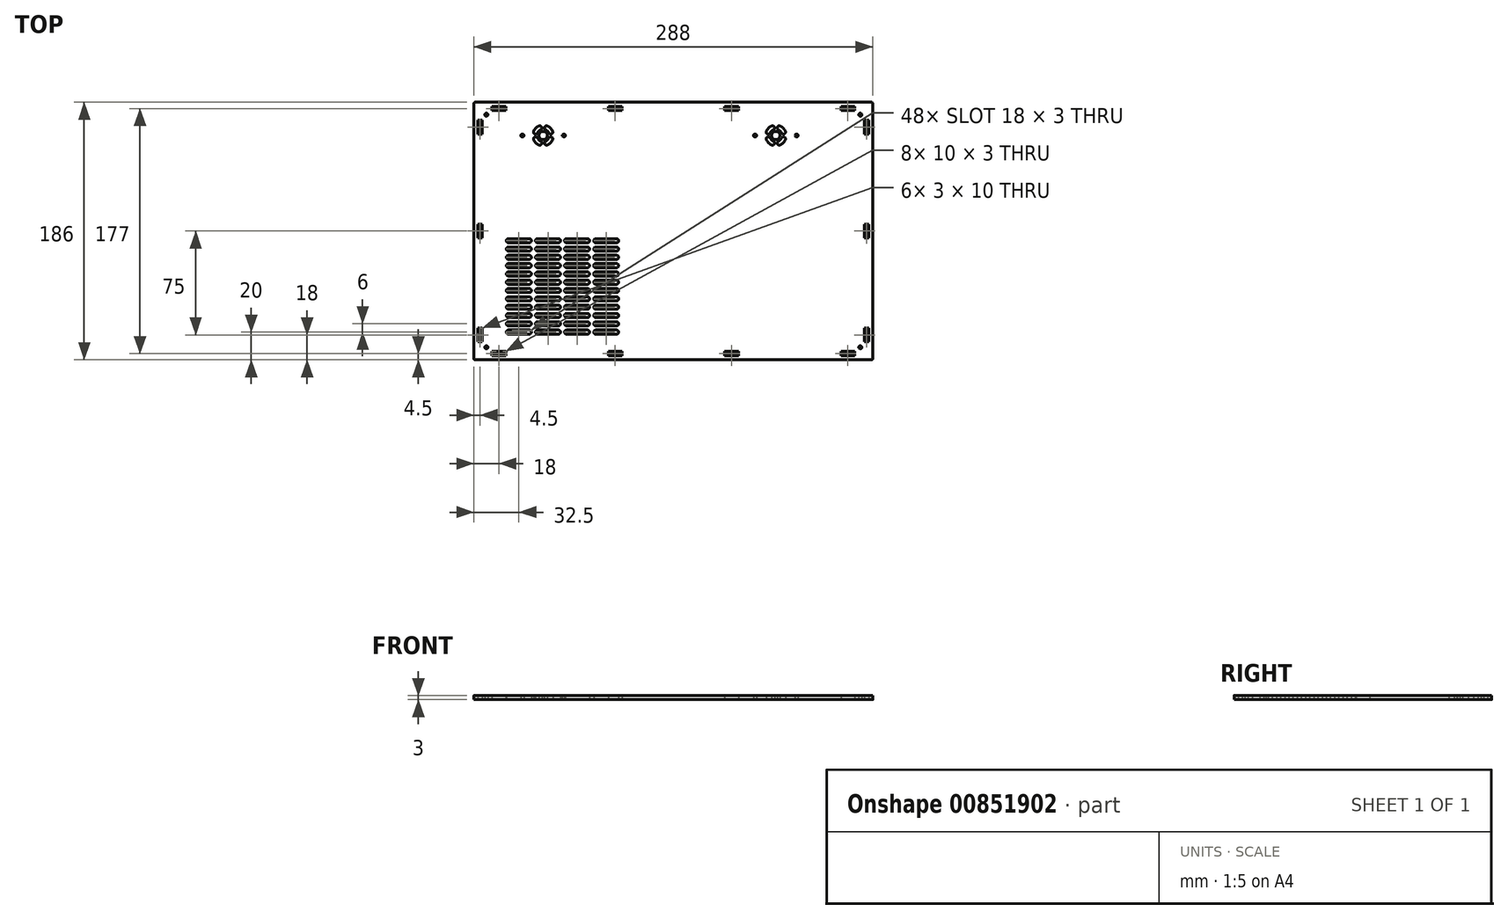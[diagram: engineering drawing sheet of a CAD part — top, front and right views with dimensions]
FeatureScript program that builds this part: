
annotation { "Feature Type Name" : "Feature", "Feature Type Description" : "" }
export const myFeature = defineFeature(function(context is Context, id is Id, definition is map)
    precondition{}
    {
        {
            var Q0;
            Q0=qCreatedBy(makeId("Top.planeOp"),FACE);
            var sketch = newSketch(context, id + "F0", { "sketchPlane" : qUnion([Q0])});
            skLineSegment(sketch, "E0.bottom", {"start": v(0, 0) * mm, "end": v(297, 0) * mm, "construction": true});
            skLineSegment(sketch, "E0.top", {"start": v(0, 210) * mm, "end": v(297, 210) * mm, "construction": true});
            skLineSegment(sketch, "E0.left", {"start": v(0, 0) * mm, "end": v(0, 210) * mm, "construction": true});
            skLineSegment(sketch, "E0.right", {"start": v(297, 0) * mm, "end": v(297, 210) * mm, "construction": true});
            skLineSegment(sketch, "E1", {"start": v(6, 5) * mm, "end": v(292, 5) * mm});
            skLineSegment(sketch, "E2", {"start": v(293, 6) * mm, "end": v(293, 190) * mm});
            skLineSegment(sketch, "E3", {"start": v(292, 191) * mm, "end": v(6, 191) * mm});
            skLineSegment(sketch, "E4", {"start": v(5, 190) * mm, "end": v(5, 6) * mm});
            skLineSegment(sketch, "E5", {"start": v(18, 8) * mm, "end": v(28, 8) * mm});
            skLineSegment(sketch, "E6", {"start": v(28, 8) * mm, "end": v(28, 11) * mm});
            skLineSegment(sketch, "E7", {"start": v(28, 11) * mm, "end": v(18, 11) * mm});
            skLineSegment(sketch, "E8", {"start": v(18, 11) * mm, "end": v(18, 8) * mm});
            skLineSegment(sketch, "E9", {"start": v(102, 8) * mm, "end": v(112, 8) * mm});
            skLineSegment(sketch, "E10", {"start": v(112, 8) * mm, "end": v(112, 11) * mm});
            skLineSegment(sketch, "E11", {"start": v(112, 11) * mm, "end": v(102, 11) * mm});
            skLineSegment(sketch, "E12", {"start": v(102, 11) * mm, "end": v(102, 8) * mm});
            skLineSegment(sketch, "E13", {"start": v(8, 18) * mm, "end": v(11, 18) * mm});
            skLineSegment(sketch, "E14", {"start": v(11, 18) * mm, "end": v(11, 28) * mm});
            skLineSegment(sketch, "E15", {"start": v(11, 28) * mm, "end": v(8, 28) * mm});
            skLineSegment(sketch, "E16", {"start": v(8, 28) * mm, "end": v(8, 18) * mm});
            skLineSegment(sketch, "E17", {"start": v(149, 5) * mm, "end": v(149, 191) * mm, "construction": true});
            skLineSegment(sketch, "E18", {"start": v(5, 98) * mm, "end": v(293, 98) * mm, "construction": true});
            skLineSegment(sketch, "E19", {"start": v(8, 98) * mm, "end": v(8, 93) * mm});
            skLineSegment(sketch, "E20", {"start": v(8, 93) * mm, "end": v(11, 93) * mm});
            skLineSegment(sketch, "E21", {"start": v(11, 93) * mm, "end": v(11, 98) * mm});
            skLineSegment(sketch, "E22.MirrorCS", {"start": v(186, 11) * mm, "end": v(196, 11) * mm});
            skLineSegment(sketch, "E23.MirrorCS", {"start": v(186, 8) * mm, "end": v(186, 11) * mm});
            skLineSegment(sketch, "E24.MirrorCS", {"start": v(196, 8) * mm, "end": v(186, 8) * mm});
            skLineSegment(sketch, "E25.MirrorCS", {"start": v(196, 11) * mm, "end": v(196, 8) * mm});
            skLineSegment(sketch, "E26.MirrorCS", {"start": v(270, 8) * mm, "end": v(270, 11) * mm});
            skLineSegment(sketch, "E27.MirrorCS", {"start": v(270, 11) * mm, "end": v(280, 11) * mm});
            skLineSegment(sketch, "E28.MirrorCS", {"start": v(280, 8) * mm, "end": v(270, 8) * mm});
            skLineSegment(sketch, "E29.MirrorCS", {"start": v(280, 11) * mm, "end": v(280, 8) * mm});
            skLineSegment(sketch, "E30.MirrorCS", {"start": v(290, 18) * mm, "end": v(287, 18) * mm});
            skLineSegment(sketch, "E31.MirrorCS", {"start": v(287, 18) * mm, "end": v(287, 28) * mm});
            skLineSegment(sketch, "E32.MirrorCS", {"start": v(290, 28) * mm, "end": v(290, 18) * mm});
            skLineSegment(sketch, "E33.MirrorCS", {"start": v(287, 28) * mm, "end": v(290, 28) * mm});
            skLineSegment(sketch, "E34.MirrorCS", {"start": v(290, 98) * mm, "end": v(290, 93) * mm});
            skLineSegment(sketch, "E35.MirrorCS", {"start": v(290, 93) * mm, "end": v(287, 93) * mm});
            skLineSegment(sketch, "E36.MirrorCS", {"start": v(287, 93) * mm, "end": v(287, 98) * mm});
            skLineSegment(sketch, "E37.MirrorCS", {"start": v(8, 98) * mm, "end": v(8, 103) * mm});
            skLineSegment(sketch, "E38.MirrorCS", {"start": v(8, 103) * mm, "end": v(11, 103) * mm});
            skLineSegment(sketch, "E39.MirrorCS", {"start": v(11, 103) * mm, "end": v(11, 98) * mm});
            skLineSegment(sketch, "E40.MirrorCS", {"start": v(11, 168) * mm, "end": v(8, 168) * mm});
            skLineSegment(sketch, "E41.MirrorCS", {"start": v(11, 178) * mm, "end": v(11, 168) * mm});
            skLineSegment(sketch, "E42.MirrorCS", {"start": v(8, 168) * mm, "end": v(8, 178) * mm});
            skLineSegment(sketch, "E43.MirrorCS", {"start": v(8, 178) * mm, "end": v(11, 178) * mm});
            skLineSegment(sketch, "E44.MirrorCS", {"start": v(18, 185) * mm, "end": v(18, 188) * mm});
            skLineSegment(sketch, "E45.MirrorCS", {"start": v(28, 185) * mm, "end": v(18, 185) * mm});
            skLineSegment(sketch, "E46.MirrorCS", {"start": v(18, 188) * mm, "end": v(28, 188) * mm});
            skLineSegment(sketch, "E47.MirrorCS", {"start": v(28, 188) * mm, "end": v(28, 185) * mm});
            skLineSegment(sketch, "E48.MirrorCS", {"start": v(102, 185) * mm, "end": v(102, 188) * mm});
            skLineSegment(sketch, "E49.MirrorCS", {"start": v(112, 185) * mm, "end": v(102, 185) * mm});
            skLineSegment(sketch, "E50.MirrorCS", {"start": v(102, 188) * mm, "end": v(112, 188) * mm});
            skLineSegment(sketch, "E51.MirrorCS", {"start": v(112, 188) * mm, "end": v(112, 185) * mm});
            skLineSegment(sketch, "E52.MirrorCS", {"start": v(186, 188) * mm, "end": v(186, 185) * mm});
            skLineSegment(sketch, "E53.MirrorCS", {"start": v(186, 185) * mm, "end": v(196, 185) * mm});
            skLineSegment(sketch, "E54.MirrorCS", {"start": v(196, 185) * mm, "end": v(196, 188) * mm});
            skLineSegment(sketch, "E55.MirrorCS", {"start": v(196, 188) * mm, "end": v(186, 188) * mm});
            skLineSegment(sketch, "E56.MirrorCS", {"start": v(270, 188) * mm, "end": v(270, 185) * mm});
            skLineSegment(sketch, "E57.MirrorCS", {"start": v(270, 185) * mm, "end": v(280, 185) * mm});
            skLineSegment(sketch, "E58.MirrorCS", {"start": v(280, 188) * mm, "end": v(270, 188) * mm});
            skLineSegment(sketch, "E59.MirrorCS", {"start": v(280, 185) * mm, "end": v(280, 188) * mm});
            skLineSegment(sketch, "E60.MirrorCS", {"start": v(290, 178) * mm, "end": v(287, 178) * mm});
            skLineSegment(sketch, "E61.MirrorCS", {"start": v(290, 168) * mm, "end": v(290, 178) * mm});
            skLineSegment(sketch, "E62.MirrorCS", {"start": v(287, 168) * mm, "end": v(290, 168) * mm});
            skLineSegment(sketch, "E63.MirrorCS", {"start": v(287, 178) * mm, "end": v(287, 168) * mm});
            skLineSegment(sketch, "E64.MirrorCS", {"start": v(287, 103) * mm, "end": v(287, 98) * mm});
            skLineSegment(sketch, "E65.MirrorCS", {"start": v(290, 103) * mm, "end": v(287, 103) * mm});
            skLineSegment(sketch, "E66.MirrorCS", {"start": v(290, 98) * mm, "end": v(290, 103) * mm});
            skLineSegment(sketch, "E67", {"start": v(30, 25) * mm, "end": v(45, 25) * mm, "construction": true});
            skArc(sketch, "E68.0.startCap", {"start": v(30, 23.5) * mm, "mid": v(28.5, 25) * mm, "end": v(30, 26.5) * mm});
            skArc(sketch, "E68.0.endCap", {"start": v(45, 26.5) * mm, "mid": v(46.5, 25) * mm, "end": v(45, 23.5) * mm});
            skLineSegment(sketch, "E68.0.left", {"start": v(30, 26.5) * mm, "end": v(45, 26.5) * mm});
            skLineSegment(sketch, "E68.0.right", {"start": v(30, 23.5) * mm, "end": v(45, 23.5) * mm});
            skLineSegment(sketch, "E69.0.1.0", {"start": v(30, 29.5) * mm, "end": v(45, 29.5) * mm});
            skLineSegment(sketch, "E69.0.1.1", {"start": v(30, 31) * mm, "end": v(45, 31) * mm, "construction": true});
            skArc(sketch, "E69.0.1.2", {"start": v(30, 29.5) * mm, "mid": v(28.5, 31) * mm, "end": v(30, 32.5) * mm});
            skLineSegment(sketch, "E69.0.1.3", {"start": v(30, 32.5) * mm, "end": v(45, 32.5) * mm});
            skArc(sketch, "E69.0.1.4", {"start": v(45, 32.5) * mm, "mid": v(46.5, 31) * mm, "end": v(45, 29.5) * mm});
            skLineSegment(sketch, "E69.0.2.0", {"start": v(30, 35.5) * mm, "end": v(45, 35.5) * mm});
            skLineSegment(sketch, "E69.0.2.1", {"start": v(30, 37) * mm, "end": v(45, 37) * mm, "construction": true});
            skArc(sketch, "E69.0.2.2", {"start": v(30, 35.5) * mm, "mid": v(28.5, 37) * mm, "end": v(30, 38.5) * mm});
            skLineSegment(sketch, "E69.0.2.3", {"start": v(30, 38.5) * mm, "end": v(45, 38.5) * mm});
            skArc(sketch, "E69.0.2.4", {"start": v(45, 38.5) * mm, "mid": v(46.5, 37) * mm, "end": v(45, 35.5) * mm});
            skLineSegment(sketch, "E69.0.3.0", {"start": v(30, 41.5) * mm, "end": v(45, 41.5) * mm});
            skLineSegment(sketch, "E69.0.3.1", {"start": v(30, 43) * mm, "end": v(45, 43) * mm, "construction": true});
            skArc(sketch, "E69.0.3.2", {"start": v(30, 41.5) * mm, "mid": v(28.5, 43) * mm, "end": v(30, 44.5) * mm});
            skLineSegment(sketch, "E69.0.3.3", {"start": v(30, 44.5) * mm, "end": v(45, 44.5) * mm});
            skArc(sketch, "E69.0.3.4", {"start": v(45, 44.5) * mm, "mid": v(46.5, 43) * mm, "end": v(45, 41.5) * mm});
            skLineSegment(sketch, "E69.0.4.0", {"start": v(30, 47.5) * mm, "end": v(45, 47.5) * mm});
            skLineSegment(sketch, "E69.0.4.1", {"start": v(30, 49) * mm, "end": v(45, 49) * mm, "construction": true});
            skArc(sketch, "E69.0.4.2", {"start": v(30, 47.5) * mm, "mid": v(28.5, 49) * mm, "end": v(30, 50.5) * mm});
            skLineSegment(sketch, "E69.0.4.3", {"start": v(30, 50.5) * mm, "end": v(45, 50.5) * mm});
            skArc(sketch, "E69.0.4.4", {"start": v(45, 50.5) * mm, "mid": v(46.5, 49) * mm, "end": v(45, 47.5) * mm});
            skLineSegment(sketch, "E69.0.5.0", {"start": v(30, 53.5) * mm, "end": v(45, 53.5) * mm});
            skLineSegment(sketch, "E69.0.5.1", {"start": v(30, 55) * mm, "end": v(45, 55) * mm, "construction": true});
            skArc(sketch, "E69.0.5.2", {"start": v(30, 53.5) * mm, "mid": v(28.5, 55) * mm, "end": v(30, 56.5) * mm});
            skLineSegment(sketch, "E69.0.5.3", {"start": v(30, 56.5) * mm, "end": v(45, 56.5) * mm});
            skArc(sketch, "E69.0.5.4", {"start": v(45, 56.5) * mm, "mid": v(46.5, 55) * mm, "end": v(45, 53.5) * mm});
            skLineSegment(sketch, "E69.0.6.0", {"start": v(30, 59.5) * mm, "end": v(45, 59.5) * mm});
            skLineSegment(sketch, "E69.0.6.1", {"start": v(30, 61) * mm, "end": v(45, 61) * mm, "construction": true});
            skArc(sketch, "E69.0.6.2", {"start": v(30, 59.5) * mm, "mid": v(28.5, 61) * mm, "end": v(30, 62.5) * mm});
            skLineSegment(sketch, "E69.0.6.3", {"start": v(30, 62.5) * mm, "end": v(45, 62.5) * mm});
            skArc(sketch, "E69.0.6.4", {"start": v(45, 62.5) * mm, "mid": v(46.5, 61) * mm, "end": v(45, 59.5) * mm});
            skLineSegment(sketch, "E69.0.7.0", {"start": v(30, 65.5) * mm, "end": v(45, 65.5) * mm});
            skLineSegment(sketch, "E69.0.7.1", {"start": v(30, 67) * mm, "end": v(45, 67) * mm, "construction": true});
            skArc(sketch, "E69.0.7.2", {"start": v(30, 65.5) * mm, "mid": v(28.5, 67) * mm, "end": v(30, 68.5) * mm});
            skLineSegment(sketch, "E69.0.7.3", {"start": v(30, 68.5) * mm, "end": v(45, 68.5) * mm});
            skArc(sketch, "E69.0.7.4", {"start": v(45, 68.5) * mm, "mid": v(46.5, 67) * mm, "end": v(45, 65.5) * mm});
            skLineSegment(sketch, "E69.0.8.0", {"start": v(30, 71.5) * mm, "end": v(45, 71.5) * mm});
            skLineSegment(sketch, "E69.0.8.1", {"start": v(30, 73) * mm, "end": v(45, 73) * mm, "construction": true});
            skArc(sketch, "E69.0.8.2", {"start": v(30, 71.5) * mm, "mid": v(28.5, 73) * mm, "end": v(30, 74.5) * mm});
            skLineSegment(sketch, "E69.0.8.3", {"start": v(30, 74.5) * mm, "end": v(45, 74.5) * mm});
            skArc(sketch, "E69.0.8.4", {"start": v(45, 74.5) * mm, "mid": v(46.5, 73) * mm, "end": v(45, 71.5) * mm});
            skLineSegment(sketch, "E69.0.9.0", {"start": v(30, 77.5) * mm, "end": v(45, 77.5) * mm});
            skLineSegment(sketch, "E69.0.9.1", {"start": v(30, 79) * mm, "end": v(45, 79) * mm, "construction": true});
            skArc(sketch, "E69.0.9.2", {"start": v(30, 77.5) * mm, "mid": v(28.5, 79) * mm, "end": v(30, 80.5) * mm});
            skLineSegment(sketch, "E69.0.9.3", {"start": v(30, 80.5) * mm, "end": v(45, 80.5) * mm});
            skArc(sketch, "E69.0.9.4", {"start": v(45, 80.5) * mm, "mid": v(46.5, 79) * mm, "end": v(45, 77.5) * mm});
            skLineSegment(sketch, "E69.1.0.0", {"start": v(51, 23.5) * mm, "end": v(66, 23.5) * mm});
            skLineSegment(sketch, "E69.1.0.1", {"start": v(51, 25) * mm, "end": v(66, 25) * mm, "construction": true});
            skArc(sketch, "E69.1.0.2", {"start": v(51, 23.5) * mm, "mid": v(49.5, 25) * mm, "end": v(51, 26.5) * mm});
            skLineSegment(sketch, "E69.1.0.3", {"start": v(51, 26.5) * mm, "end": v(66, 26.5) * mm});
            skArc(sketch, "E69.1.0.4", {"start": v(66, 26.5) * mm, "mid": v(67.5, 25) * mm, "end": v(66, 23.5) * mm});
            skLineSegment(sketch, "E69.1.1.0", {"start": v(51, 29.5) * mm, "end": v(66, 29.5) * mm});
            skLineSegment(sketch, "E69.1.1.1", {"start": v(51, 31) * mm, "end": v(66, 31) * mm, "construction": true});
            skArc(sketch, "E69.1.1.2", {"start": v(51, 29.5) * mm, "mid": v(49.5, 31) * mm, "end": v(51, 32.5) * mm});
            skLineSegment(sketch, "E69.1.1.3", {"start": v(51, 32.5) * mm, "end": v(66, 32.5) * mm});
            skArc(sketch, "E69.1.1.4", {"start": v(66, 32.5) * mm, "mid": v(67.5, 31) * mm, "end": v(66, 29.5) * mm});
            skLineSegment(sketch, "E69.1.2.0", {"start": v(51, 35.5) * mm, "end": v(66, 35.5) * mm});
            skLineSegment(sketch, "E69.1.2.1", {"start": v(51, 37) * mm, "end": v(66, 37) * mm, "construction": true});
            skArc(sketch, "E69.1.2.2", {"start": v(51, 35.5) * mm, "mid": v(49.5, 37) * mm, "end": v(51, 38.5) * mm});
            skLineSegment(sketch, "E69.1.2.3", {"start": v(51, 38.5) * mm, "end": v(66, 38.5) * mm});
            skArc(sketch, "E69.1.2.4", {"start": v(66, 38.5) * mm, "mid": v(67.5, 37) * mm, "end": v(66, 35.5) * mm});
            skLineSegment(sketch, "E69.1.3.0", {"start": v(51, 41.5) * mm, "end": v(66, 41.5) * mm});
            skLineSegment(sketch, "E69.1.3.1", {"start": v(51, 43) * mm, "end": v(66, 43) * mm, "construction": true});
            skArc(sketch, "E69.1.3.2", {"start": v(51, 41.5) * mm, "mid": v(49.5, 43) * mm, "end": v(51, 44.5) * mm});
            skLineSegment(sketch, "E69.1.3.3", {"start": v(51, 44.5) * mm, "end": v(66, 44.5) * mm});
            skArc(sketch, "E69.1.3.4", {"start": v(66, 44.5) * mm, "mid": v(67.5, 43) * mm, "end": v(66, 41.5) * mm});
            skLineSegment(sketch, "E69.1.4.0", {"start": v(51, 47.5) * mm, "end": v(66, 47.5) * mm});
            skLineSegment(sketch, "E69.1.4.1", {"start": v(51, 49) * mm, "end": v(66, 49) * mm, "construction": true});
            skArc(sketch, "E69.1.4.2", {"start": v(51, 47.5) * mm, "mid": v(49.5, 49) * mm, "end": v(51, 50.5) * mm});
            skLineSegment(sketch, "E69.1.4.3", {"start": v(51, 50.5) * mm, "end": v(66, 50.5) * mm});
            skArc(sketch, "E69.1.4.4", {"start": v(66, 50.5) * mm, "mid": v(67.5, 49) * mm, "end": v(66, 47.5) * mm});
            skLineSegment(sketch, "E69.1.5.0", {"start": v(51, 53.5) * mm, "end": v(66, 53.5) * mm});
            skLineSegment(sketch, "E69.1.5.1", {"start": v(51, 55) * mm, "end": v(66, 55) * mm, "construction": true});
            skArc(sketch, "E69.1.5.2", {"start": v(51, 53.5) * mm, "mid": v(49.5, 55) * mm, "end": v(51, 56.5) * mm});
            skLineSegment(sketch, "E69.1.5.3", {"start": v(51, 56.5) * mm, "end": v(66, 56.5) * mm});
            skArc(sketch, "E69.1.5.4", {"start": v(66, 56.5) * mm, "mid": v(67.5, 55) * mm, "end": v(66, 53.5) * mm});
            skLineSegment(sketch, "E69.1.6.0", {"start": v(51, 59.5) * mm, "end": v(66, 59.5) * mm});
            skLineSegment(sketch, "E69.1.6.1", {"start": v(51, 61) * mm, "end": v(66, 61) * mm, "construction": true});
            skArc(sketch, "E69.1.6.2", {"start": v(51, 59.5) * mm, "mid": v(49.5, 61) * mm, "end": v(51, 62.5) * mm});
            skLineSegment(sketch, "E69.1.6.3", {"start": v(51, 62.5) * mm, "end": v(66, 62.5) * mm});
            skArc(sketch, "E69.1.6.4", {"start": v(66, 62.5) * mm, "mid": v(67.5, 61) * mm, "end": v(66, 59.5) * mm});
            skLineSegment(sketch, "E69.1.7.0", {"start": v(51, 65.5) * mm, "end": v(66, 65.5) * mm});
            skLineSegment(sketch, "E69.1.7.1", {"start": v(51, 67) * mm, "end": v(66, 67) * mm, "construction": true});
            skArc(sketch, "E69.1.7.2", {"start": v(51, 65.5) * mm, "mid": v(49.5, 67) * mm, "end": v(51, 68.5) * mm});
            skLineSegment(sketch, "E69.1.7.3", {"start": v(51, 68.5) * mm, "end": v(66, 68.5) * mm});
            skArc(sketch, "E69.1.7.4", {"start": v(66, 68.5) * mm, "mid": v(67.5, 67) * mm, "end": v(66, 65.5) * mm});
            skLineSegment(sketch, "E69.1.8.0", {"start": v(51, 71.5) * mm, "end": v(66, 71.5) * mm});
            skLineSegment(sketch, "E69.1.8.1", {"start": v(51, 73) * mm, "end": v(66, 73) * mm, "construction": true});
            skArc(sketch, "E69.1.8.2", {"start": v(51, 71.5) * mm, "mid": v(49.5, 73) * mm, "end": v(51, 74.5) * mm});
            skLineSegment(sketch, "E69.1.8.3", {"start": v(51, 74.5) * mm, "end": v(66, 74.5) * mm});
            skArc(sketch, "E69.1.8.4", {"start": v(66, 74.5) * mm, "mid": v(67.5, 73) * mm, "end": v(66, 71.5) * mm});
            skLineSegment(sketch, "E69.1.9.0", {"start": v(51, 77.5) * mm, "end": v(66, 77.5) * mm});
            skLineSegment(sketch, "E69.1.9.1", {"start": v(51, 79) * mm, "end": v(66, 79) * mm, "construction": true});
            skArc(sketch, "E69.1.9.2", {"start": v(51, 77.5) * mm, "mid": v(49.5, 79) * mm, "end": v(51, 80.5) * mm});
            skLineSegment(sketch, "E69.1.9.3", {"start": v(51, 80.5) * mm, "end": v(66, 80.5) * mm});
            skArc(sketch, "E69.1.9.4", {"start": v(66, 80.5) * mm, "mid": v(67.5, 79) * mm, "end": v(66, 77.5) * mm});
            skLineSegment(sketch, "E69.2.0.0", {"start": v(72, 23.5) * mm, "end": v(87, 23.5) * mm});
            skLineSegment(sketch, "E69.2.0.1", {"start": v(72, 25) * mm, "end": v(87, 25) * mm, "construction": true});
            skArc(sketch, "E69.2.0.2", {"start": v(72, 23.5) * mm, "mid": v(70.5, 25) * mm, "end": v(72, 26.5) * mm});
            skLineSegment(sketch, "E69.2.0.3", {"start": v(72, 26.5) * mm, "end": v(87, 26.5) * mm});
            skArc(sketch, "E69.2.0.4", {"start": v(87, 26.5) * mm, "mid": v(88.5, 25) * mm, "end": v(87, 23.5) * mm});
            skLineSegment(sketch, "E69.2.1.0", {"start": v(72, 29.5) * mm, "end": v(87, 29.5) * mm});
            skLineSegment(sketch, "E69.2.1.1", {"start": v(72, 31) * mm, "end": v(87, 31) * mm, "construction": true});
            skArc(sketch, "E69.2.1.2", {"start": v(72, 29.5) * mm, "mid": v(70.5, 31) * mm, "end": v(72, 32.5) * mm});
            skLineSegment(sketch, "E69.2.1.3", {"start": v(72, 32.5) * mm, "end": v(87, 32.5) * mm});
            skArc(sketch, "E69.2.1.4", {"start": v(87, 32.5) * mm, "mid": v(88.5, 31) * mm, "end": v(87, 29.5) * mm});
            skLineSegment(sketch, "E69.2.2.0", {"start": v(72, 35.5) * mm, "end": v(87, 35.5) * mm});
            skLineSegment(sketch, "E69.2.2.1", {"start": v(72, 37) * mm, "end": v(87, 37) * mm, "construction": true});
            skArc(sketch, "E69.2.2.2", {"start": v(72, 35.5) * mm, "mid": v(70.5, 37) * mm, "end": v(72, 38.5) * mm});
            skLineSegment(sketch, "E69.2.2.3", {"start": v(72, 38.5) * mm, "end": v(87, 38.5) * mm});
            skArc(sketch, "E69.2.2.4", {"start": v(87, 38.5) * mm, "mid": v(88.5, 37) * mm, "end": v(87, 35.5) * mm});
            skLineSegment(sketch, "E69.2.3.0", {"start": v(72, 41.5) * mm, "end": v(87, 41.5) * mm});
            skLineSegment(sketch, "E69.2.3.1", {"start": v(72, 43) * mm, "end": v(87, 43) * mm, "construction": true});
            skArc(sketch, "E69.2.3.2", {"start": v(72, 41.5) * mm, "mid": v(70.5, 43) * mm, "end": v(72, 44.5) * mm});
            skLineSegment(sketch, "E69.2.3.3", {"start": v(72, 44.5) * mm, "end": v(87, 44.5) * mm});
            skArc(sketch, "E69.2.3.4", {"start": v(87, 44.5) * mm, "mid": v(88.5, 43) * mm, "end": v(87, 41.5) * mm});
            skLineSegment(sketch, "E69.2.4.0", {"start": v(72, 47.5) * mm, "end": v(87, 47.5) * mm});
            skLineSegment(sketch, "E69.2.4.1", {"start": v(72, 49) * mm, "end": v(87, 49) * mm, "construction": true});
            skArc(sketch, "E69.2.4.2", {"start": v(72, 47.5) * mm, "mid": v(70.5, 49) * mm, "end": v(72, 50.5) * mm});
            skLineSegment(sketch, "E69.2.4.3", {"start": v(72, 50.5) * mm, "end": v(87, 50.5) * mm});
            skArc(sketch, "E69.2.4.4", {"start": v(87, 50.5) * mm, "mid": v(88.5, 49) * mm, "end": v(87, 47.5) * mm});
            skLineSegment(sketch, "E69.2.5.0", {"start": v(72, 53.5) * mm, "end": v(87, 53.5) * mm});
            skLineSegment(sketch, "E69.2.5.1", {"start": v(72, 55) * mm, "end": v(87, 55) * mm, "construction": true});
            skArc(sketch, "E69.2.5.2", {"start": v(72, 53.5) * mm, "mid": v(70.5, 55) * mm, "end": v(72, 56.5) * mm});
            skLineSegment(sketch, "E69.2.5.3", {"start": v(72, 56.5) * mm, "end": v(87, 56.5) * mm});
            skArc(sketch, "E69.2.5.4", {"start": v(87, 56.5) * mm, "mid": v(88.5, 55) * mm, "end": v(87, 53.5) * mm});
            skLineSegment(sketch, "E69.2.6.0", {"start": v(72, 59.5) * mm, "end": v(87, 59.5) * mm});
            skLineSegment(sketch, "E69.2.6.1", {"start": v(72, 61) * mm, "end": v(87, 61) * mm, "construction": true});
            skArc(sketch, "E69.2.6.2", {"start": v(72, 59.5) * mm, "mid": v(70.5, 61) * mm, "end": v(72, 62.5) * mm});
            skLineSegment(sketch, "E69.2.6.3", {"start": v(72, 62.5) * mm, "end": v(87, 62.5) * mm});
            skArc(sketch, "E69.2.6.4", {"start": v(87, 62.5) * mm, "mid": v(88.5, 61) * mm, "end": v(87, 59.5) * mm});
            skLineSegment(sketch, "E69.2.7.0", {"start": v(72, 65.5) * mm, "end": v(87, 65.5) * mm});
            skLineSegment(sketch, "E69.2.7.1", {"start": v(72, 67) * mm, "end": v(87, 67) * mm, "construction": true});
            skArc(sketch, "E69.2.7.2", {"start": v(72, 65.5) * mm, "mid": v(70.5, 67) * mm, "end": v(72, 68.5) * mm});
            skLineSegment(sketch, "E69.2.7.3", {"start": v(72, 68.5) * mm, "end": v(87, 68.5) * mm});
            skArc(sketch, "E69.2.7.4", {"start": v(87, 68.5) * mm, "mid": v(88.5, 67) * mm, "end": v(87, 65.5) * mm});
            skLineSegment(sketch, "E69.2.8.0", {"start": v(72, 71.5) * mm, "end": v(87, 71.5) * mm});
            skLineSegment(sketch, "E69.2.8.1", {"start": v(72, 73) * mm, "end": v(87, 73) * mm, "construction": true});
            skArc(sketch, "E69.2.8.2", {"start": v(72, 71.5) * mm, "mid": v(70.5, 73) * mm, "end": v(72, 74.5) * mm});
            skLineSegment(sketch, "E69.2.8.3", {"start": v(72, 74.5) * mm, "end": v(87, 74.5) * mm});
            skArc(sketch, "E69.2.8.4", {"start": v(87, 74.5) * mm, "mid": v(88.5, 73) * mm, "end": v(87, 71.5) * mm});
            skLineSegment(sketch, "E69.2.9.0", {"start": v(72, 77.5) * mm, "end": v(87, 77.5) * mm});
            skLineSegment(sketch, "E69.2.9.1", {"start": v(72, 79) * mm, "end": v(87, 79) * mm, "construction": true});
            skArc(sketch, "E69.2.9.2", {"start": v(72, 77.5) * mm, "mid": v(70.5, 79) * mm, "end": v(72, 80.5) * mm});
            skLineSegment(sketch, "E69.2.9.3", {"start": v(72, 80.5) * mm, "end": v(87, 80.5) * mm});
            skArc(sketch, "E69.2.9.4", {"start": v(87, 80.5) * mm, "mid": v(88.5, 79) * mm, "end": v(87, 77.5) * mm});
            skLineSegment(sketch, "E69.3.0.0", {"start": v(93, 23.5) * mm, "end": v(108, 23.5) * mm});
            skLineSegment(sketch, "E69.3.0.1", {"start": v(93, 25) * mm, "end": v(108, 25) * mm, "construction": true});
            skArc(sketch, "E69.3.0.2", {"start": v(93, 23.5) * mm, "mid": v(91.5, 25) * mm, "end": v(93, 26.5) * mm});
            skLineSegment(sketch, "E69.3.0.3", {"start": v(93, 26.5) * mm, "end": v(108, 26.5) * mm});
            skArc(sketch, "E69.3.0.4", {"start": v(108, 26.5) * mm, "mid": v(109.5, 25) * mm, "end": v(108, 23.5) * mm});
            skLineSegment(sketch, "E69.3.1.0", {"start": v(93, 29.5) * mm, "end": v(108, 29.5) * mm});
            skLineSegment(sketch, "E69.3.1.1", {"start": v(93, 31) * mm, "end": v(108, 31) * mm, "construction": true});
            skArc(sketch, "E69.3.1.2", {"start": v(93, 29.5) * mm, "mid": v(91.5, 31) * mm, "end": v(93, 32.5) * mm});
            skLineSegment(sketch, "E69.3.1.3", {"start": v(93, 32.5) * mm, "end": v(108, 32.5) * mm});
            skArc(sketch, "E69.3.1.4", {"start": v(108, 32.5) * mm, "mid": v(109.5, 31) * mm, "end": v(108, 29.5) * mm});
            skLineSegment(sketch, "E69.3.2.0", {"start": v(93, 35.5) * mm, "end": v(108, 35.5) * mm});
            skLineSegment(sketch, "E69.3.2.1", {"start": v(93, 37) * mm, "end": v(108, 37) * mm, "construction": true});
            skArc(sketch, "E69.3.2.2", {"start": v(93, 35.5) * mm, "mid": v(91.5, 37) * mm, "end": v(93, 38.5) * mm});
            skLineSegment(sketch, "E69.3.2.3", {"start": v(93, 38.5) * mm, "end": v(108, 38.5) * mm});
            skArc(sketch, "E69.3.2.4", {"start": v(108, 38.5) * mm, "mid": v(109.5, 37) * mm, "end": v(108, 35.5) * mm});
            skLineSegment(sketch, "E69.3.3.0", {"start": v(93, 41.5) * mm, "end": v(108, 41.5) * mm});
            skLineSegment(sketch, "E69.3.3.1", {"start": v(93, 43) * mm, "end": v(108, 43) * mm, "construction": true});
            skArc(sketch, "E69.3.3.2", {"start": v(93, 41.5) * mm, "mid": v(91.5, 43) * mm, "end": v(93, 44.5) * mm});
            skLineSegment(sketch, "E69.3.3.3", {"start": v(93, 44.5) * mm, "end": v(108, 44.5) * mm});
            skArc(sketch, "E69.3.3.4", {"start": v(108, 44.5) * mm, "mid": v(109.5, 43) * mm, "end": v(108, 41.5) * mm});
            skLineSegment(sketch, "E69.3.4.0", {"start": v(93, 47.5) * mm, "end": v(108, 47.5) * mm});
            skLineSegment(sketch, "E69.3.4.1", {"start": v(93, 49) * mm, "end": v(108, 49) * mm, "construction": true});
            skArc(sketch, "E69.3.4.2", {"start": v(93, 47.5) * mm, "mid": v(91.5, 49) * mm, "end": v(93, 50.5) * mm});
            skLineSegment(sketch, "E69.3.4.3", {"start": v(93, 50.5) * mm, "end": v(108, 50.5) * mm});
            skArc(sketch, "E69.3.4.4", {"start": v(108, 50.5) * mm, "mid": v(109.5, 49) * mm, "end": v(108, 47.5) * mm});
            skLineSegment(sketch, "E69.3.5.0", {"start": v(93, 53.5) * mm, "end": v(108, 53.5) * mm});
            skLineSegment(sketch, "E69.3.5.1", {"start": v(93, 55) * mm, "end": v(108, 55) * mm, "construction": true});
            skArc(sketch, "E69.3.5.2", {"start": v(93, 53.5) * mm, "mid": v(91.5, 55) * mm, "end": v(93, 56.5) * mm});
            skLineSegment(sketch, "E69.3.5.3", {"start": v(93, 56.5) * mm, "end": v(108, 56.5) * mm});
            skArc(sketch, "E69.3.5.4", {"start": v(108, 56.5) * mm, "mid": v(109.5, 55) * mm, "end": v(108, 53.5) * mm});
            skLineSegment(sketch, "E69.3.6.0", {"start": v(93, 59.5) * mm, "end": v(108, 59.5) * mm});
            skLineSegment(sketch, "E69.3.6.1", {"start": v(93, 61) * mm, "end": v(108, 61) * mm, "construction": true});
            skArc(sketch, "E69.3.6.2", {"start": v(93, 59.5) * mm, "mid": v(91.5, 61) * mm, "end": v(93, 62.5) * mm});
            skLineSegment(sketch, "E69.3.6.3", {"start": v(93, 62.5) * mm, "end": v(108, 62.5) * mm});
            skArc(sketch, "E69.3.6.4", {"start": v(108, 62.5) * mm, "mid": v(109.5, 61) * mm, "end": v(108, 59.5) * mm});
            skLineSegment(sketch, "E69.3.7.0", {"start": v(93, 65.5) * mm, "end": v(108, 65.5) * mm});
            skLineSegment(sketch, "E69.3.7.1", {"start": v(93, 67) * mm, "end": v(108, 67) * mm, "construction": true});
            skArc(sketch, "E69.3.7.2", {"start": v(93, 65.5) * mm, "mid": v(91.5, 67) * mm, "end": v(93, 68.5) * mm});
            skLineSegment(sketch, "E69.3.7.3", {"start": v(93, 68.5) * mm, "end": v(108, 68.5) * mm});
            skArc(sketch, "E69.3.7.4", {"start": v(108, 68.5) * mm, "mid": v(109.5, 67) * mm, "end": v(108, 65.5) * mm});
            skLineSegment(sketch, "E69.3.8.0", {"start": v(93, 71.5) * mm, "end": v(108, 71.5) * mm});
            skLineSegment(sketch, "E69.3.8.1", {"start": v(93, 73) * mm, "end": v(108, 73) * mm, "construction": true});
            skArc(sketch, "E69.3.8.2", {"start": v(93, 71.5) * mm, "mid": v(91.5, 73) * mm, "end": v(93, 74.5) * mm});
            skLineSegment(sketch, "E69.3.8.3", {"start": v(93, 74.5) * mm, "end": v(108, 74.5) * mm});
            skArc(sketch, "E69.3.8.4", {"start": v(108, 74.5) * mm, "mid": v(109.5, 73) * mm, "end": v(108, 71.5) * mm});
            skLineSegment(sketch, "E69.3.9.0", {"start": v(93, 77.5) * mm, "end": v(108, 77.5) * mm});
            skLineSegment(sketch, "E69.3.9.1", {"start": v(93, 79) * mm, "end": v(108, 79) * mm, "construction": true});
            skArc(sketch, "E69.3.9.2", {"start": v(93, 77.5) * mm, "mid": v(91.5, 79) * mm, "end": v(93, 80.5) * mm});
            skLineSegment(sketch, "E69.3.9.3", {"start": v(93, 80.5) * mm, "end": v(108, 80.5) * mm});
            skArc(sketch, "E69.3.9.4", {"start": v(108, 80.5) * mm, "mid": v(109.5, 79) * mm, "end": v(108, 77.5) * mm});
            skLineSegment(sketch, "E69.direction1", {"start": v(30, 23.5) * mm, "end": v(51, 23.5) * mm, "construction": true});
            skLineSegment(sketch, "E69.direction2", {"start": v(30, 23.5) * mm, "end": v(30, 29.5) * mm, "construction": true});
            skLineSegment(sketch, "E70.0.0.10", {"start": v(30, 83.5) * mm, "end": v(45, 83.5) * mm});
            skLineSegment(sketch, "E70.3.0.10", {"start": v(30, 85) * mm, "end": v(45, 85) * mm, "construction": true});
            skArc(sketch, "E70.6.0.10", {"start": v(30, 83.5) * mm, "mid": v(28.5, 85) * mm, "end": v(30, 86.5) * mm});
            skLineSegment(sketch, "E70.10.0.10", {"start": v(30, 86.5) * mm, "end": v(45, 86.5) * mm});
            skArc(sketch, "E70.13.0.10", {"start": v(45, 86.5) * mm, "mid": v(46.5, 85) * mm, "end": v(45, 83.5) * mm});
            skLineSegment(sketch, "E70.0.0.11", {"start": v(30, 89.5) * mm, "end": v(45, 89.5) * mm});
            skLineSegment(sketch, "E70.3.0.11", {"start": v(30, 91) * mm, "end": v(45, 91) * mm, "construction": true});
            skArc(sketch, "E70.6.0.11", {"start": v(30, 89.5) * mm, "mid": v(28.5, 91) * mm, "end": v(30, 92.5) * mm});
            skLineSegment(sketch, "E70.10.0.11", {"start": v(30, 92.5) * mm, "end": v(45, 92.5) * mm});
            skArc(sketch, "E70.13.0.11", {"start": v(45, 92.5) * mm, "mid": v(46.5, 91) * mm, "end": v(45, 89.5) * mm});
            skLineSegment(sketch, "E70.0.1.10", {"start": v(51, 83.5) * mm, "end": v(66, 83.5) * mm});
            skLineSegment(sketch, "E70.3.1.10", {"start": v(51, 85) * mm, "end": v(66, 85) * mm, "construction": true});
            skArc(sketch, "E70.6.1.10", {"start": v(51, 83.5) * mm, "mid": v(49.5, 85) * mm, "end": v(51, 86.5) * mm});
            skLineSegment(sketch, "E70.10.1.10", {"start": v(51, 86.5) * mm, "end": v(66, 86.5) * mm});
            skArc(sketch, "E70.13.1.10", {"start": v(66, 86.5) * mm, "mid": v(67.5, 85) * mm, "end": v(66, 83.5) * mm});
            skLineSegment(sketch, "E70.0.1.11", {"start": v(51, 89.5) * mm, "end": v(66, 89.5) * mm});
            skLineSegment(sketch, "E70.3.1.11", {"start": v(51, 91) * mm, "end": v(66, 91) * mm, "construction": true});
            skArc(sketch, "E70.6.1.11", {"start": v(51, 89.5) * mm, "mid": v(49.5, 91) * mm, "end": v(51, 92.5) * mm});
            skLineSegment(sketch, "E70.10.1.11", {"start": v(51, 92.5) * mm, "end": v(66, 92.5) * mm});
            skArc(sketch, "E70.13.1.11", {"start": v(66, 92.5) * mm, "mid": v(67.5, 91) * mm, "end": v(66, 89.5) * mm});
            skLineSegment(sketch, "E70.0.2.10", {"start": v(72, 83.5) * mm, "end": v(87, 83.5) * mm});
            skLineSegment(sketch, "E70.3.2.10", {"start": v(72, 85) * mm, "end": v(87, 85) * mm, "construction": true});
            skArc(sketch, "E70.6.2.10", {"start": v(72, 83.5) * mm, "mid": v(70.5, 85) * mm, "end": v(72, 86.5) * mm});
            skLineSegment(sketch, "E70.10.2.10", {"start": v(72, 86.5) * mm, "end": v(87, 86.5) * mm});
            skArc(sketch, "E70.13.2.10", {"start": v(87, 86.5) * mm, "mid": v(88.5, 85) * mm, "end": v(87, 83.5) * mm});
            skLineSegment(sketch, "E70.0.2.11", {"start": v(72, 89.5) * mm, "end": v(87, 89.5) * mm});
            skLineSegment(sketch, "E70.3.2.11", {"start": v(72, 91) * mm, "end": v(87, 91) * mm, "construction": true});
            skArc(sketch, "E70.6.2.11", {"start": v(72, 89.5) * mm, "mid": v(70.5, 91) * mm, "end": v(72, 92.5) * mm});
            skLineSegment(sketch, "E70.10.2.11", {"start": v(72, 92.5) * mm, "end": v(87, 92.5) * mm});
            skArc(sketch, "E70.13.2.11", {"start": v(87, 92.5) * mm, "mid": v(88.5, 91) * mm, "end": v(87, 89.5) * mm});
            skLineSegment(sketch, "E70.0.3.10", {"start": v(93, 83.5) * mm, "end": v(108, 83.5) * mm});
            skLineSegment(sketch, "E70.3.3.10", {"start": v(93, 85) * mm, "end": v(108, 85) * mm, "construction": true});
            skArc(sketch, "E70.6.3.10", {"start": v(93, 83.5) * mm, "mid": v(91.5, 85) * mm, "end": v(93, 86.5) * mm});
            skLineSegment(sketch, "E70.10.3.10", {"start": v(93, 86.5) * mm, "end": v(108, 86.5) * mm});
            skArc(sketch, "E70.13.3.10", {"start": v(108, 86.5) * mm, "mid": v(109.5, 85) * mm, "end": v(108, 83.5) * mm});
            skLineSegment(sketch, "E70.0.3.11", {"start": v(93, 89.5) * mm, "end": v(108, 89.5) * mm});
            skLineSegment(sketch, "E70.3.3.11", {"start": v(93, 91) * mm, "end": v(108, 91) * mm, "construction": true});
            skArc(sketch, "E70.6.3.11", {"start": v(93, 89.5) * mm, "mid": v(91.5, 91) * mm, "end": v(93, 92.5) * mm});
            skLineSegment(sketch, "E70.10.3.11", {"start": v(93, 92.5) * mm, "end": v(108, 92.5) * mm});
            skArc(sketch, "E70.13.3.11", {"start": v(108, 92.5) * mm, "mid": v(109.5, 91) * mm, "end": v(108, 89.5) * mm});
            skCircle(sketch, "E71", {"center": v(55, 167) * mm, "radius": 3 * mm});
            skLineSegment(sketch, "E72", {"start": v(40, 167) * mm, "end": v(70, 167) * mm, "construction": true});
            skCircle(sketch, "E73", {"center": v(40, 167) * mm, "radius": 1.1 * mm});
            skCircle(sketch, "E74", {"center": v(70, 167) * mm, "radius": 1.1 * mm});
            skArc(sketch, "E75", {"start": v(49.52, 169.44) * mm, "mid": v(50.76, 171.24) * mm, "end": v(52.56, 172.48) * mm, "construction": true});
            skLineSegment(sketch, "E76", {"start": v(55, 176) * mm, "end": v(55, 158) * mm, "construction": true});
            skLineSegment(sketch, "E77", {"start": v(55, 167) * mm, "end": v(49.52, 169.44) * mm, "construction": true});
            skLineSegment(sketch, "E78", {"start": v(55, 167) * mm, "end": v(52.56, 172.48) * mm, "construction": true});
            skArc(sketch, "E79.0.startCap", {"start": v(50.89, 168.83) * mm, "mid": v(48.9, 168.07) * mm, "end": v(48.15, 170.05) * mm});
            skArc(sketch, "E79.0.endCap", {"start": v(51.95, 173.85) * mm, "mid": v(53.93, 173.1) * mm, "end": v(53.17, 171.11) * mm});
            skArc(sketch, "E79.0.left", {"start": v(48.15, 170.05) * mm, "mid": v(49.7, 172.3) * mm, "end": v(51.95, 173.85) * mm});
            skArc(sketch, "E79.0.right", {"start": v(50.89, 168.83) * mm, "mid": v(51.82, 170.18) * mm, "end": v(53.17, 171.11) * mm});
            skArc(sketch, "E80.MirrorCS", {"start": v(49.52, 164.56) * mm, "mid": v(50.76, 162.76) * mm, "end": v(52.56, 161.52) * mm, "construction": true});
            skArc(sketch, "E81.MirrorCS", {"start": v(50.89, 165.17) * mm, "mid": v(48.9, 165.93) * mm, "end": v(48.15, 163.95) * mm});
            skArc(sketch, "E82.MirrorCS", {"start": v(50.89, 165.17) * mm, "mid": v(51.82, 163.82) * mm, "end": v(53.17, 162.89) * mm});
            skArc(sketch, "E83.MirrorCS", {"start": v(51.95, 160.15) * mm, "mid": v(53.93, 160.9) * mm, "end": v(53.17, 162.89) * mm});
            skArc(sketch, "E84.MirrorCS", {"start": v(48.15, 163.95) * mm, "mid": v(49.7, 161.7) * mm, "end": v(51.95, 160.15) * mm});
            skArc(sketch, "E85.MirrorCS", {"start": v(58.05, 160.15) * mm, "mid": v(56.07, 160.9) * mm, "end": v(56.83, 162.89) * mm});
            skArc(sketch, "E86.MirrorCS", {"start": v(61.85, 170.05) * mm, "mid": v(60.3, 172.3) * mm, "end": v(58.05, 173.85) * mm});
            skArc(sketch, "E87.MirrorCS", {"start": v(59.11, 165.17) * mm, "mid": v(58.18, 163.82) * mm, "end": v(56.83, 162.89) * mm});
            skArc(sketch, "E88.MirrorCS", {"start": v(59.11, 168.83) * mm, "mid": v(58.18, 170.18) * mm, "end": v(56.83, 171.11) * mm});
            skArc(sketch, "E89.MirrorCS", {"start": v(61.85, 163.95) * mm, "mid": v(60.3, 161.7) * mm, "end": v(58.05, 160.15) * mm});
            skArc(sketch, "E90.MirrorCS", {"start": v(60.48, 169.44) * mm, "mid": v(59.24, 171.24) * mm, "end": v(57.44, 172.48) * mm, "construction": true});
            skArc(sketch, "E91.MirrorCS", {"start": v(58.05, 173.85) * mm, "mid": v(56.07, 173.1) * mm, "end": v(56.83, 171.11) * mm});
            skArc(sketch, "E92.MirrorCS", {"start": v(60.48, 164.56) * mm, "mid": v(59.24, 162.76) * mm, "end": v(57.44, 161.52) * mm, "construction": true});
            skArc(sketch, "E93.MirrorCS", {"start": v(59.11, 168.83) * mm, "mid": v(61.1, 168.07) * mm, "end": v(61.85, 170.05) * mm});
            skArc(sketch, "E94.MirrorCS", {"start": v(59.11, 165.17) * mm, "mid": v(61.1, 165.93) * mm, "end": v(61.85, 163.95) * mm});
            skCircle(sketch, "E95", {"center": v(223, 167) * mm, "radius": 3 * mm});
            skLineSegment(sketch, "E96", {"start": v(208, 167) * mm, "end": v(238, 167) * mm, "construction": true});
            skCircle(sketch, "E97", {"center": v(208, 167) * mm, "radius": 1.1 * mm});
            skCircle(sketch, "E98", {"center": v(238, 167) * mm, "radius": 1.1 * mm});
            skArc(sketch, "E99", {"start": v(217.52, 169.44) * mm, "mid": v(218.76, 171.24) * mm, "end": v(220.56, 172.48) * mm, "construction": true});
            skLineSegment(sketch, "E100", {"start": v(223, 176) * mm, "end": v(223, 158) * mm, "construction": true});
            skLineSegment(sketch, "E101", {"start": v(223, 167) * mm, "end": v(217.52, 169.44) * mm, "construction": true});
            skLineSegment(sketch, "E102", {"start": v(223, 167) * mm, "end": v(220.56, 172.48) * mm, "construction": true});
            skArc(sketch, "E103.0.startCap", {"start": v(218.89, 168.83) * mm, "mid": v(216.9, 168.07) * mm, "end": v(216.15, 170.05) * mm});
            skArc(sketch, "E103.0.endCap", {"start": v(219.95, 173.85) * mm, "mid": v(221.93, 173.1) * mm, "end": v(221.17, 171.11) * mm});
            skArc(sketch, "E103.0.left", {"start": v(216.15, 170.05) * mm, "mid": v(217.7, 172.3) * mm, "end": v(219.95, 173.85) * mm});
            skArc(sketch, "E103.0.right", {"start": v(218.89, 168.83) * mm, "mid": v(219.82, 170.18) * mm, "end": v(221.17, 171.11) * mm});
            skArc(sketch, "E104.MirrorCS", {"start": v(217.52, 164.56) * mm, "mid": v(218.76, 162.76) * mm, "end": v(220.56, 161.52) * mm, "construction": true});
            skArc(sketch, "E105.MirrorCS", {"start": v(218.89, 165.17) * mm, "mid": v(216.9, 165.93) * mm, "end": v(216.15, 163.95) * mm});
            skArc(sketch, "E106.MirrorCS", {"start": v(218.89, 165.17) * mm, "mid": v(219.82, 163.82) * mm, "end": v(221.17, 162.89) * mm});
            skArc(sketch, "E107.MirrorCS", {"start": v(219.95, 160.15) * mm, "mid": v(221.93, 160.9) * mm, "end": v(221.17, 162.89) * mm});
            skArc(sketch, "E108.MirrorCS", {"start": v(216.15, 163.95) * mm, "mid": v(217.7, 161.7) * mm, "end": v(219.95, 160.15) * mm});
            skArc(sketch, "E109.MirrorCS", {"start": v(226.05, 160.15) * mm, "mid": v(224.07, 160.9) * mm, "end": v(224.83, 162.89) * mm});
            skArc(sketch, "E110.MirrorCS", {"start": v(229.85, 170.05) * mm, "mid": v(228.3, 172.3) * mm, "end": v(226.05, 173.85) * mm});
            skArc(sketch, "E111.MirrorCS", {"start": v(227.11, 165.17) * mm, "mid": v(226.18, 163.82) * mm, "end": v(224.83, 162.89) * mm});
            skArc(sketch, "E112.MirrorCS", {"start": v(227.11, 168.83) * mm, "mid": v(226.18, 170.18) * mm, "end": v(224.83, 171.11) * mm});
            skArc(sketch, "E113.MirrorCS", {"start": v(229.85, 163.95) * mm, "mid": v(228.3, 161.7) * mm, "end": v(226.05, 160.15) * mm});
            skArc(sketch, "E114.MirrorCS", {"start": v(228.48, 169.44) * mm, "mid": v(227.24, 171.24) * mm, "end": v(225.44, 172.48) * mm, "construction": true});
            skArc(sketch, "E115.MirrorCS", {"start": v(226.05, 173.85) * mm, "mid": v(224.07, 173.1) * mm, "end": v(224.83, 171.11) * mm});
            skArc(sketch, "E116.MirrorCS", {"start": v(228.48, 164.56) * mm, "mid": v(227.24, 162.76) * mm, "end": v(225.44, 161.52) * mm, "construction": true});
            skArc(sketch, "E117.MirrorCS", {"start": v(227.11, 168.83) * mm, "mid": v(229.1, 168.07) * mm, "end": v(229.85, 170.05) * mm});
            skArc(sketch, "E118.MirrorCS", {"start": v(227.11, 165.17) * mm, "mid": v(229.1, 165.93) * mm, "end": v(229.85, 163.95) * mm});
            skPoint(sketch, "E119.visualSharp", {"position": v(5, 5) * mm});
            skArc(sketch, "E119.filletArc", {"start": v(5, 6) * mm, "mid": v(5.3, 5.3) * mm, "end": v(6, 5) * mm});
            skPoint(sketch, "E120.visualSharp", {"position": v(5, 191) * mm});
            skArc(sketch, "E120.filletArc", {"start": v(6, 191) * mm, "mid": v(5.3, 190.7) * mm, "end": v(5, 190) * mm});
            skPoint(sketch, "E121.visualSharp", {"position": v(293, 191) * mm});
            skArc(sketch, "E121.filletArc", {"start": v(293, 190) * mm, "mid": v(292.7, 190.7) * mm, "end": v(292, 191) * mm});
            skPoint(sketch, "E122.visualSharp", {"position": v(293, 5) * mm});
            skArc(sketch, "E122.filletArc", {"start": v(292, 5) * mm, "mid": v(292.7, 5.3) * mm, "end": v(293, 6) * mm});
            skCircle(sketch, "E123", {"center": v(14, 14) * mm, "radius": 1.1 * mm});
            skCircle(sketch, "E124", {"center": v(14, 182) * mm, "radius": 1.1 * mm});
            skCircle(sketch, "E125", {"center": v(284, 14) * mm, "radius": 1.1 * mm});
            skCircle(sketch, "E126", {"center": v(284, 182) * mm, "radius": 1.1 * mm});
            skSolve(sketch);
        }
        {
            var Q0;
            Q0=makeQuery(id+"F0.imprint","IMPRINT",FACE,{"disambiguationData":[TD([[makeQuery(id+"F0.imprint","IMPRINT",EDGE,{"derivedFrom":sQuery(id+"F0.wireOp",EDGE,"E1")}),1.0]])]});
            extrude(context, id + "F1", {"entities" : qUnion([Q0]), "depth" : 3 * mm, "offsetDistance" : 25 * mm});
        }
    });
